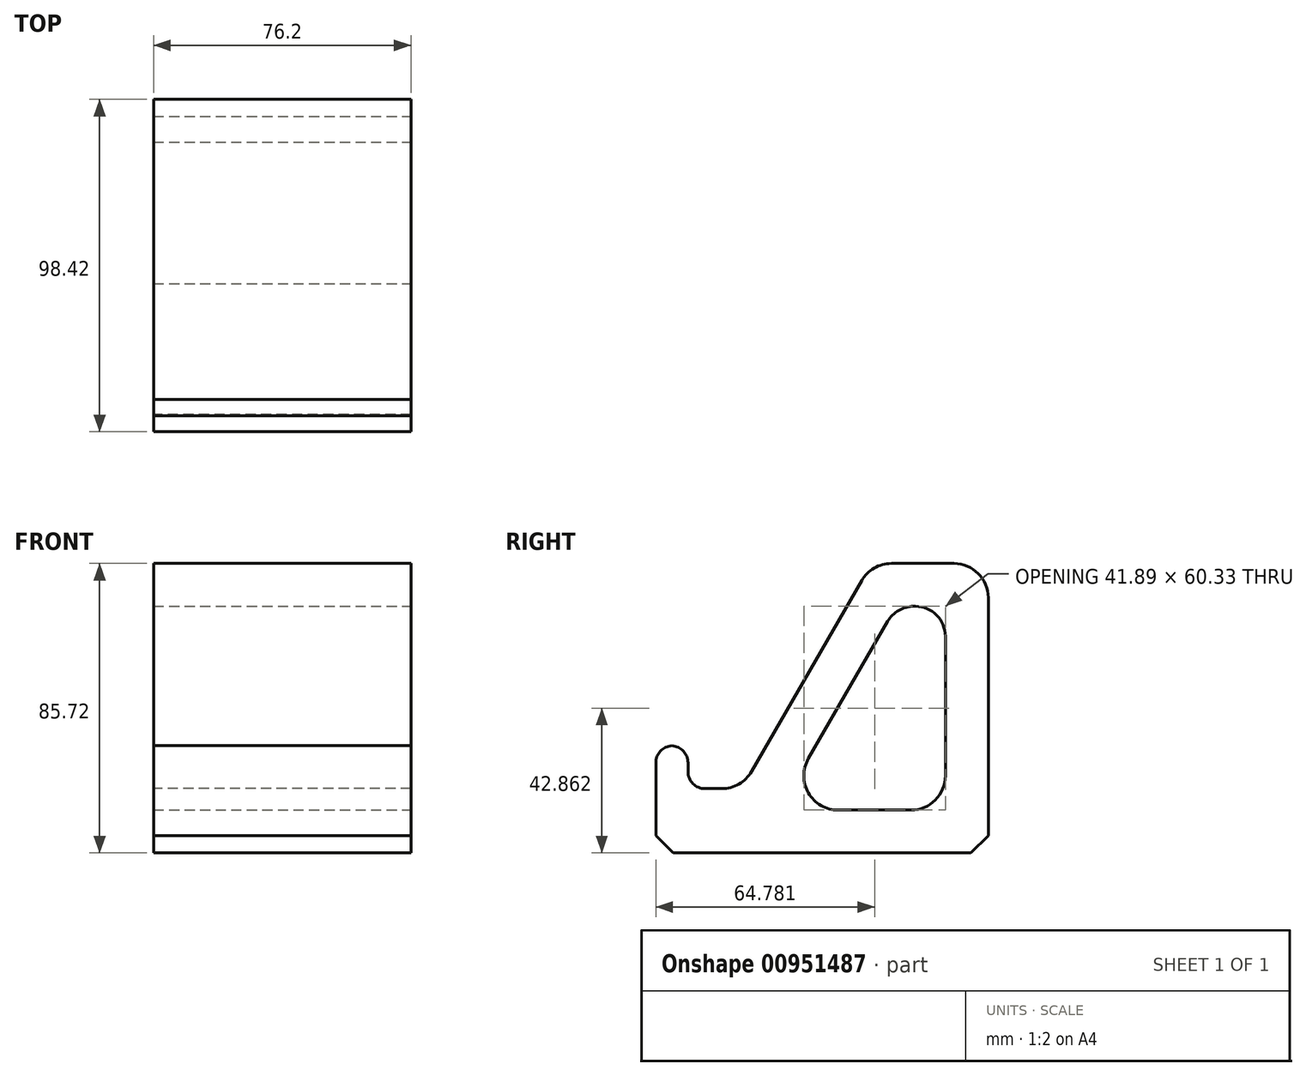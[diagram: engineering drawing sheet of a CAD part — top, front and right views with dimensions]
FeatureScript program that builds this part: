
annotation { "Feature Type Name" : "Feature", "Feature Type Description" : "" }
export const myFeature = defineFeature(function(context is Context, id is Id, definition is map)
    precondition{}
    {
        {
            var Q0;
            Q0=qCreatedBy(makeId("Right.planeOp"),FACE);
            var sketch = newSketch(context, id + "F0", { "sketchPlane" : qUnion([Q0])});
            skLineSegment(sketch, "E0", {"start": v(-12.7, 0) * mm, "end": v(12.7, 0) * mm});
            skLineSegment(sketch, "E1", {"start": v(12.7, 0) * mm, "end": v(56.7, 76.2) * mm});
            skLineSegment(sketch, "E2", {"start": v(56.7, 76.2) * mm, "end": v(76.2, 76.2) * mm});
            skLineSegment(sketch, "E3", {"start": v(-12.7, 0) * mm, "end": v(-12.7, 31.75) * mm});
            skLineSegment(sketch, "E4", {"start": v(76.2, 76.2) * mm, "end": v(76.2, 0) * mm});
            skLineSegment(sketch, "E5.0", {"start": v(-3.18, 9.53) * mm, "end": v(-3.18, 31.75) * mm});
            skLineSegment(sketch, "E5.1", {"start": v(85.73, 85.73) * mm, "end": v(85.73, 0) * mm});
            skLineSegment(sketch, "E5.2", {"start": v(51.2, 85.73) * mm, "end": v(85.72, 85.73) * mm});
            skLineSegment(sketch, "E5.3", {"start": v(7.2, 9.52) * mm, "end": v(51.2, 85.73) * mm});
            skLineSegment(sketch, "E5.4", {"start": v(-3.18, 9.53) * mm, "end": v(7.2, 9.53) * mm});
            skLineSegment(sketch, "E6", {"start": v(85.73, 0) * mm, "end": v(76.2, 0) * mm});
            skLineSegment(sketch, "E7", {"start": v(-3.18, 31.75) * mm, "end": v(-12.7, 31.75) * mm});
            skLineSegment(sketch, "E8", {"start": v(-3.18, 19.05) * mm, "end": v(12.7, 19.05) * mm});
            skSolve(sketch);
        }
        {
            var Q0;
            Q0 = qSketchRegion(id + "F0", true);
            extrude(context, id + "F1", {"entities" : qUnion([Q0]), "endBound" : BoundingType.SYMMETRIC, "depth" : 76.2 * mm, "offsetDistance" : 25.4 * mm});
        }
        {
            var Q0;
            Q0=makeQuery(id+"F1.opExtrude","CAP_FACE",FACE,{"disambiguationData":[OSD([sQuery(id+"F0.wireOp",EDGE,"E0"),sQuery(id+"F0.wireOp",EDGE,"E1"),sQuery(id+"F0.wireOp",EDGE,"E2"),sQuery(id+"F0.wireOp",EDGE,"E3"),sQuery(id+"F0.wireOp",EDGE,"E4"),sQuery(id+"F0.wireOp",EDGE,"E5.0"),sQuery(id+"F0.wireOp",EDGE,"E5.1"),sQuery(id+"F0.wireOp",EDGE,"E5.2"),sQuery(id+"F0.wireOp",EDGE,"E5.3"),sQuery(id+"F0.wireOp",EDGE,"E5.4"),sQuery(id+"F0.wireOp",EDGE,"E6"),sQuery(id+"F0.wireOp",EDGE,"E7")])],"isStart":false});
            var sketch = newSketch(context, id + "F2", { "sketchPlane" : qUnion([Q0])});
            skLineSegment(sketch, "E9", {"start": v(12.7, 0) * mm, "end": v(76.2, 0) * mm});
            skLineSegment(sketch, "E10", {"start": v(12.7, 0) * mm, "end": v(56.7, 76.2) * mm});
            skLineSegment(sketch, "E11", {"start": v(56.7, 76.2) * mm, "end": v(76.2, 76.2) * mm});
            skLineSegment(sketch, "E12", {"start": v(76.2, 76.2) * mm, "end": v(76.2, 0) * mm});
            skSolve(sketch);
        }
        {
            var Q0;
            Q0=makeQuery(id+"F2.imprint","IMPRINT",FACE,{"disambiguationData":[TD([[makeQuery(id+"F2.imprint","IMPRINT",EDGE,{"derivedFrom":sQuery(id+"F2.wireOp",EDGE,"E9")}),1.0]])]});
            var Q1;
            Q1=makeQuery(id+"F1.opExtrude","CAP_FACE",FACE,{"disambiguationData":[OSD([sQuery(id+"F0.wireOp",EDGE,"E0"),sQuery(id+"F0.wireOp",EDGE,"E1"),sQuery(id+"F0.wireOp",EDGE,"E2"),sQuery(id+"F0.wireOp",EDGE,"E3"),sQuery(id+"F0.wireOp",EDGE,"E4"),sQuery(id+"F0.wireOp",EDGE,"E5.0"),sQuery(id+"F0.wireOp",EDGE,"E5.1"),sQuery(id+"F0.wireOp",EDGE,"E5.2"),sQuery(id+"F0.wireOp",EDGE,"E5.3"),sQuery(id+"F0.wireOp",EDGE,"E5.4"),sQuery(id+"F0.wireOp",EDGE,"E6"),sQuery(id+"F0.wireOp",EDGE,"E7")])],"isStart":true});
            extrude(context, id + "F3", {"entities" : qUnion([Q0]), "operationType" : NewBodyOperationType.ADD, "endBound" : BoundingType.UP_TO_SURFACE, "oppositeDirection" : true, "depth" : 94.8 * mm, "endBoundEntityFace" : qUnion([Q1]), "offsetDistance" : 25.4 * mm});
        }
        {
            var Q0;
            Q0=makeQuery(id+"F3.boolean.opBoolean","MERGE",FACE,{"derivedFrom":[makeQuery(id+"F1.opExtrude","CAP_FACE",FACE,{"disambiguationData":[OSD([sQuery(id+"F0.wireOp",EDGE,"E0"),sQuery(id+"F0.wireOp",EDGE,"E1"),sQuery(id+"F0.wireOp",EDGE,"E2"),sQuery(id+"F0.wireOp",EDGE,"E3"),sQuery(id+"F0.wireOp",EDGE,"E4"),sQuery(id+"F0.wireOp",EDGE,"E5.0"),sQuery(id+"F0.wireOp",EDGE,"E5.1"),sQuery(id+"F0.wireOp",EDGE,"E5.2"),sQuery(id+"F0.wireOp",EDGE,"E5.3"),sQuery(id+"F0.wireOp",EDGE,"E6"),sQuery(id+"F0.wireOp",EDGE,"E7"),sQuery(id+"F0.wireOp",EDGE,"E8")])],"isStart":false}),makeQuery(id+"F3.opExtrude","CAP_FACE",FACE,{"disambiguationData":[OSD([sQuery(id+"F2.wireOp",EDGE,"E9"),sQuery(id+"F2.wireOp",EDGE,"E10"),sQuery(id+"F2.wireOp",EDGE,"E11"),sQuery(id+"F2.wireOp",EDGE,"E12")])],"isStart":true})]});
            var sketch = newSketch(context, id + "F4", { "sketchPlane" : qUnion([Q0])});
            skLineSegment(sketch, "E13.0", {"start": v(23.7, 12.7) * mm, "end": v(73.03, 12.7) * mm});
            skLineSegment(sketch, "E13.1", {"start": v(73.03, 73.03) * mm, "end": v(73.03, 12.7) * mm});
            skLineSegment(sketch, "E13.2", {"start": v(58.53, 73.03) * mm, "end": v(73.03, 73.03) * mm});
            skLineSegment(sketch, "E13.3", {"start": v(23.7, 12.7) * mm, "end": v(58.53, 73.03) * mm});
            skSolve(sketch);
        }
        {
            var Q0;
            Q0=makeQuery(id+"F4.imprint","IMPRINT",FACE,{"disambiguationData":[TD([[makeQuery(id+"F4.imprint","IMPRINT",EDGE,{"derivedFrom":sQuery(id+"F4.wireOp",EDGE,"E13.0")}),1.0]])]});
            extrude(context, id + "F5", {"entities" : qUnion([Q0]), "operationType" : NewBodyOperationType.REMOVE, "endBound" : BoundingType.THROUGH_ALL, "oppositeDirection" : true, "depth" : 25.4 * mm, "offsetDistance" : 25.4 * mm});
        }
        {
            var Q0;
            Q0=makeQuery(id+"F1.opExtrude","SWEPT_EDGE",EDGE,{"disambiguationData":[OSD([sQuery(id+"F0.wireOp",EDGE,"E5.0"),sQuery(id+"F0.wireOp",EDGE,"E8")])]});
            var Q1;
            Q1=makeQuery(id+"F1.opExtrude","SWEPT_EDGE",EDGE,{"disambiguationData":[OSD([sQuery(id+"F0.wireOp",EDGE,"E5.0"),sQuery(id+"F0.wireOp",EDGE,"E7")])]});
            var Q2;
            Q2=makeQuery(id+"F1.opExtrude","SWEPT_EDGE",EDGE,{"disambiguationData":[OSD([sQuery(id+"F0.wireOp",EDGE,"E3"),sQuery(id+"F0.wireOp",EDGE,"E7")])]});
            fillet(context, id + "F6", {"entities" : qUnion([Q0, Q1, Q2]), "radius" : 5.08 * mm, "tangentPropagation" : true, "allowEdgeOverflow" : false});
        }
        {
            var Q0;
            Q0=makeQuery(id+"F1.opExtrude","SWEPT_EDGE",EDGE,{"disambiguationData":[OSD([sQuery(id+"F0.wireOp",EDGE,"E5.3"),sQuery(id+"F0.wireOp",EDGE,"E8")])]});
            var Q1;
            Q1=makeQuery(id+"F1.opExtrude","SWEPT_EDGE",EDGE,{"disambiguationData":[OSD([sQuery(id+"F0.wireOp",EDGE,"E5.2"),sQuery(id+"F0.wireOp",EDGE,"E5.3")])]});
            var Q2;
            Q2=makeQuery(id+"F1.opExtrude","SWEPT_EDGE",EDGE,{"disambiguationData":[OSD([sQuery(id+"F0.wireOp",EDGE,"E5.1"),sQuery(id+"F0.wireOp",EDGE,"E5.2")])]});
            var Q3;
            Q3=makeQuery(id+"F5.boolean.opBoolean","COPY",EDGE,{"derivedFrom":makeQuery(id+"F5.opExtrude","SWEPT_EDGE",EDGE,{"disambiguationData":[OSD([sQuery(id+"F4.wireOp",EDGE,"E13.0"),sQuery(id+"F4.wireOp",EDGE,"E13.3")])]})});
            var Q4;
            Q4=makeQuery(id+"F5.boolean.opBoolean","COPY",EDGE,{"derivedFrom":makeQuery(id+"F5.opExtrude","SWEPT_EDGE",EDGE,{"disambiguationData":[OSD([sQuery(id+"F4.wireOp",EDGE,"E13.0"),sQuery(id+"F4.wireOp",EDGE,"E13.1")])]})});
            fillet(context, id + "F7", {"entities" : qUnion([Q0, Q1, Q2, Q3, Q4]), "radius" : 10.16 * mm, "tangentPropagation" : true, "allowEdgeOverflow" : false});
        }
        {
            var Q0;
            Q0=makeQuery(id+"F1.opExtrude","SWEPT_EDGE",EDGE,{"disambiguationData":[OSD([sQuery(id+"F0.wireOp",EDGE,"E5.1"),sQuery(id+"F0.wireOp",EDGE,"E6")])]});
            var Q1;
            Q1=makeQuery(id+"F1.opExtrude","SWEPT_EDGE",EDGE,{"disambiguationData":[OSD([sQuery(id+"F0.wireOp",EDGE,"E0"),sQuery(id+"F0.wireOp",EDGE,"E3")])]});
            chamfer(context, id + "F8", {"entities" : qUnion([Q0, Q1]), "width" : 5.08 * mm, "tangentPropagation" : true});
        }
        {
            var Q0;
            Q0=makeQuery(id+"F5.boolean.opBoolean","COPY",EDGE,{"derivedFrom":makeQuery(id+"F5.opExtrude","SWEPT_EDGE",EDGE,{"disambiguationData":[OSD([sQuery(id+"F4.wireOp",EDGE,"E13.1"),sQuery(id+"F4.wireOp",EDGE,"E13.2")])]})});
            var Q1;
            Q1=makeQuery(id+"F5.boolean.opBoolean","COPY",EDGE,{"derivedFrom":makeQuery(id+"F5.opExtrude","SWEPT_EDGE",EDGE,{"disambiguationData":[OSD([sQuery(id+"F4.wireOp",EDGE,"E13.2"),sQuery(id+"F4.wireOp",EDGE,"E13.3")])]})});
            fillet(context, id + "F9", {"entities" : qUnion([Q0, Q1]), "radius" : 8.9 * mm, "tangentPropagation" : true, "allowEdgeOverflow" : false});
        }
    });
